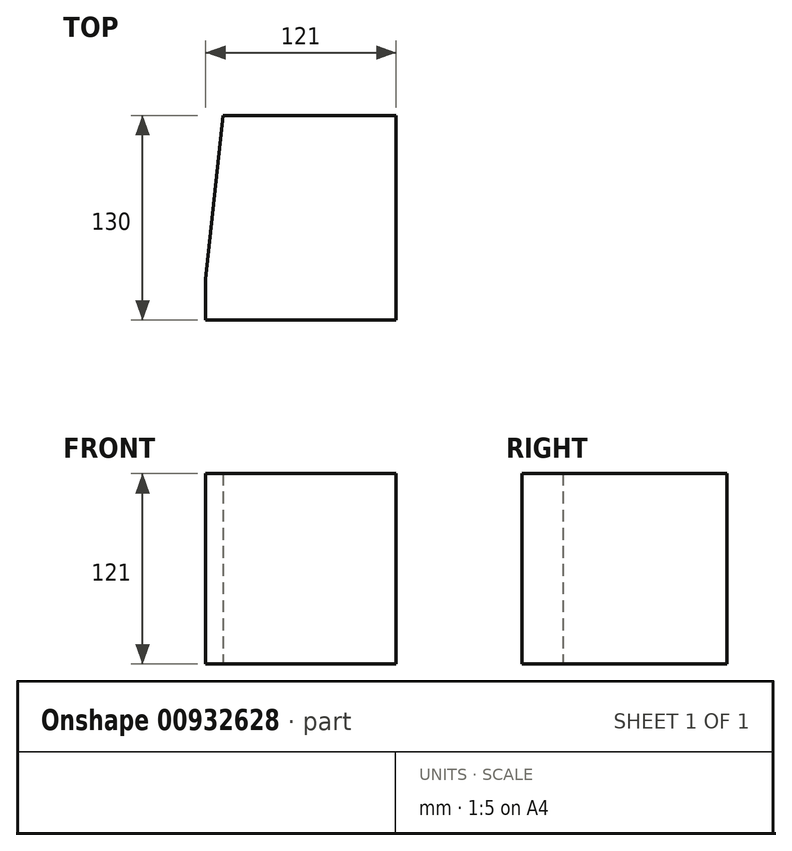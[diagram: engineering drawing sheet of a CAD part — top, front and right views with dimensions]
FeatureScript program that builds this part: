
annotation { "Feature Type Name" : "Feature", "Feature Type Description" : "" }
export const myFeature = defineFeature(function(context is Context, id is Id, definition is map)
    precondition{}
    {
        {
            var Q0;
            Q0=qCreatedBy(makeId("Top.planeOp"),FACE);
            var sketch = newSketch(context, id + "F0", { "sketchPlane" : qUnion([Q0])});
            skLineSegment(sketch, "E0.bottom", {"start": v(0, 0) * mm, "end": v(121, 0) * mm});
            skLineSegment(sketch, "E0.top", {"start": v(11, 130) * mm, "end": v(121, 130) * mm});
            skLineSegment(sketch, "E0.right", {"start": v(121, 0) * mm, "end": v(121, 130) * mm});
            skLineSegment(sketch, "E1", {"start": v(0, 0) * mm, "end": v(0, 26) * mm});
            skLineSegment(sketch, "E2", {"start": v(11, 130) * mm, "end": v(0, 26) * mm});
            skSolve(sketch);
        }
        {
            var Q0;
            Q0=makeQuery(id+"F0.imprint","IMPRINT",FACE,{"disambiguationData":[TD([[makeQuery(id+"F0.imprint","IMPRINT",EDGE,{"derivedFrom":sQuery(id+"F0.wireOp",EDGE,"E0.bottom")}),1.0]])]});
            extrude(context, id + "F1", {"entities" : qUnion([Q0]), "depth" : 121 * mm, "offsetDistance" : 25 * mm});
        }
    });
